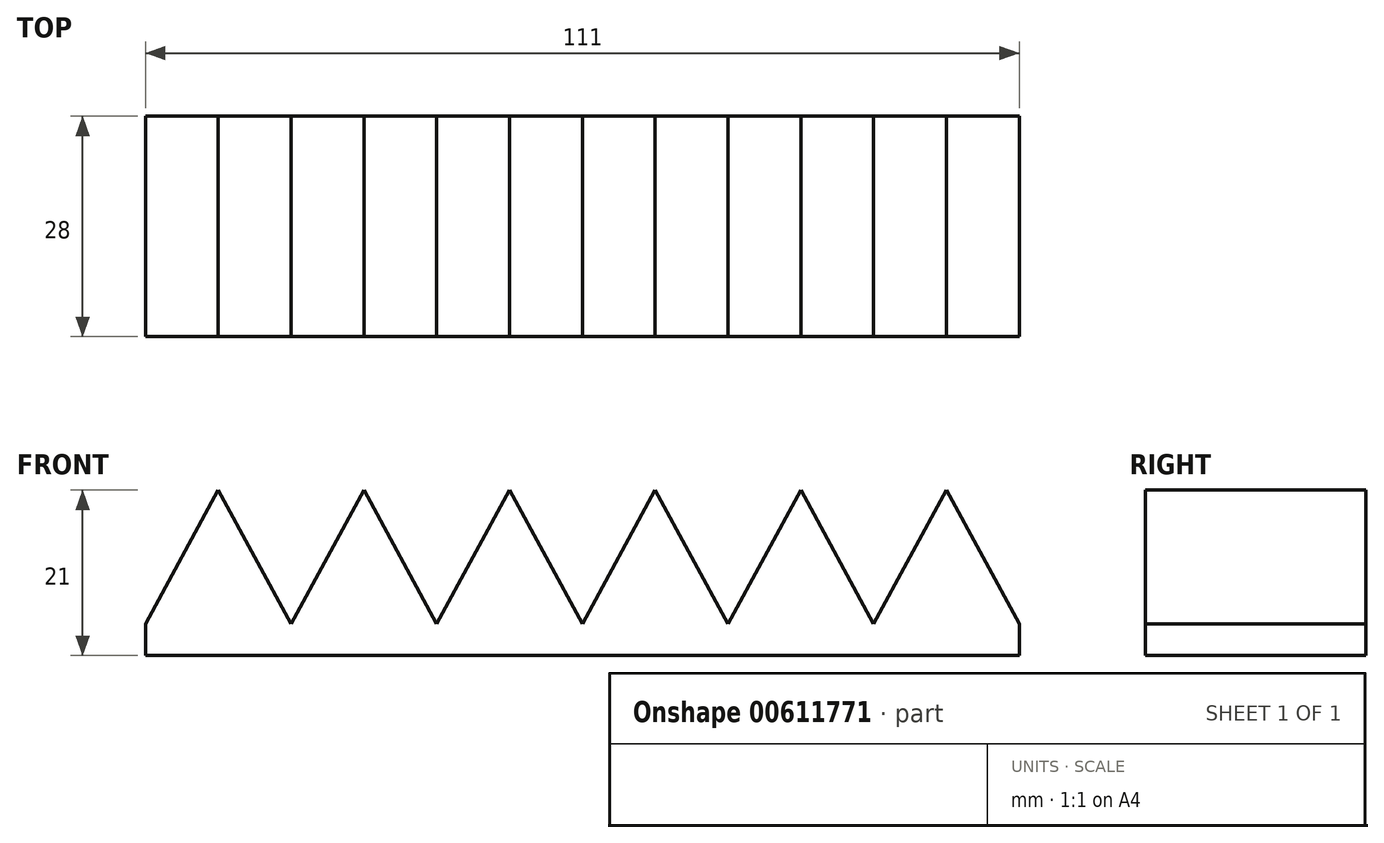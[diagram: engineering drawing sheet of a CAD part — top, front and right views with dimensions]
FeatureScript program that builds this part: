
annotation { "Feature Type Name" : "Feature", "Feature Type Description" : "" }
export const myFeature = defineFeature(function(context is Context, id is Id, definition is map)
    precondition{}
    {
        {
            var Q0;
            Q0=qCreatedBy(makeId("Front.planeOp"),FACE);
            var sketch = newSketch(context, id + "F0", { "sketchPlane" : qUnion([Q0])});
            skLineSegment(sketch, "E0.bottom", {"start": v(-39.26, -23.56) * mm, "end": v(71.74, -23.56) * mm});
            skLineSegment(sketch, "E0.left", {"start": v(-39.26, -23.56) * mm, "end": v(-39.26, -19.56) * mm});
            skLineSegment(sketch, "E0.right", {"start": v(71.74, -23.56) * mm, "end": v(71.74, -19.56) * mm});
            skLineSegment(sketch, "E1", {"start": v(-39.26, -19.56) * mm, "end": v(-30.01, -2.56) * mm});
            skLineSegment(sketch, "E2", {"start": v(-30.01, -2.56) * mm, "end": v(-20.76, -19.56) * mm});
            skLineSegment(sketch, "E3", {"start": v(-20.76, -19.56) * mm, "end": v(-11.51, -2.56) * mm});
            skLineSegment(sketch, "E4", {"start": v(-11.51, -2.56) * mm, "end": v(-2.26, -19.56) * mm});
            skLineSegment(sketch, "E5", {"start": v(-2.26, -19.56) * mm, "end": v(6.99, -2.56) * mm});
            skLineSegment(sketch, "E6", {"start": v(6.99, -2.56) * mm, "end": v(16.24, -19.56) * mm});
            skLineSegment(sketch, "E7", {"start": v(16.24, -19.56) * mm, "end": v(25.49, -2.56) * mm});
            skLineSegment(sketch, "E8", {"start": v(25.49, -2.56) * mm, "end": v(34.74, -19.56) * mm});
            skLineSegment(sketch, "E9", {"start": v(34.74, -19.56) * mm, "end": v(43.99, -2.56) * mm});
            skLineSegment(sketch, "E10", {"start": v(43.99, -2.56) * mm, "end": v(53.24, -19.56) * mm});
            skLineSegment(sketch, "E11", {"start": v(53.24, -19.56) * mm, "end": v(62.49, -2.56) * mm});
            skLineSegment(sketch, "E12", {"start": v(62.49, -2.56) * mm, "end": v(71.74, -19.56) * mm});
            skPoint(sketch, "E13.orphan", {"position": v(-39.26, -2.56) * mm});
            skSolve(sketch);
        }
        {
            var Q0;
            Q0=makeQuery(id+"F0.imprint","IMPRINT",FACE,{"disambiguationData":[TD([[makeQuery(id+"F0.imprint","IMPRINT",EDGE,{"derivedFrom":sQuery(id+"F0.wireOp",EDGE,"E0.bottom")}),1.0]])]});
            extrude(context, id + "F1", {"entities" : qUnion([Q0]), "depth" : 28 * mm, "offsetDistance" : 25 * mm});
        }
    });
